# Revit family: ВКО прес_турбо_Eng
name_source: partatom
category: Mechanical Equipment
units: mm (PartAtom-declared; Revit-internal decimal feet)

## family parameters
Always vertical = Yes
Classification = None
Cut with Voids When Loaded = No
Part Type = Normal
Room Calculation Point = No
Round Connector Dimension = Use Diameter
Shared = No
Work Plane-Based = No

## types (6) — shared parameters
00_20_Manufacturer = Vents
00_20_Name = Axial fan
Casing Material = Plastic, opaque, white
Frequency = 50 Hz
Load Classification = HVAC
Maintenance zone material = <By Category>
Manufacturer = Vents
Number of Fase = 1
URL = https://ventilation-system.com
Voltage = 230 V
zero-valued in all types: Default Elevation

## per-type parameters (varying)
| type | Amperage | Apparent Load | D | D1 | Diameter | Dy | L | L1 | Length | Maximum Air Flow | Power | R | R1 | Ry | Sound pressure level at 3 m distance | Weight |
| 100 VKO press | 0.100 A | 23 W | 100 mm  [stored 0.328084 ft] | 104 mm | 100 mm  [stored 0.328084 ft] | 98 mm  [stored 0.321522 ft] | 91 mm  [stored 0.298556 ft] | 31 mm  [stored 0.101706 ft] | 91 mm  [stored 0.298556 ft] | 106.0 m³/h | 16 W | 50 mm  [stored 0.164042 ft] | 52 mm | 49 mm  [stored 0.160761 ft] | 39 dBA | 0.41 kg |
| 125 VKO press | 0.105 A | 24 W | 125 mm  [stored 0.410105 ft] | 129 mm | 125 mm  [stored 0.410105 ft] | 123 mm  [stored 0.403543 ft] | 93 mm  [stored 0.305118 ft] | 31 mm  [stored 0.101706 ft] | 93 mm  [stored 0.305118 ft] | 192.0 m³/h | 24 W | 63 mm | 65 mm | 62 mm | 39 dBA | 0.48 kg |
| 150 VKO press | 0.130 A | 30 W | 150 mm | 154 mm  [stored 0.505249 ft] | 150 mm | 148 mm  [stored 0.485564 ft] | 108 mm  [stored 0.354331 ft] | 46 mm  [stored 0.150919 ft] | 108 mm  [stored 0.354331 ft] | 312.0 m³/h | 29 W | 75 mm | 77 mm  [stored 0.252625 ft] | 74 mm  [stored 0.242782 ft] | 44 dBA | 0.80 kg |
| 100 VKO turbo | 0.100 A | 23 W | 100 mm  [stored 0.328084 ft] | 104 mm | 100 mm  [stored 0.328084 ft] | 98 mm  [stored 0.321522 ft] | 91 mm  [stored 0.298556 ft] | 31 mm  [stored 0.101706 ft] | 91 mm  [stored 0.298556 ft] | 135.0 m³/h | 16 W | 50 mm  [stored 0.164042 ft] | 52 mm | 49 mm  [stored 0.160761 ft] | 38 dBA | 0.41 kg |
| 125 VKO turbo | 0.105 A | 24 W | 125 mm  [stored 0.410105 ft] | 129 mm | 125 mm  [stored 0.410105 ft] | 123 mm  [stored 0.403543 ft] | 93 mm  [stored 0.305118 ft] | 31 mm  [stored 0.101706 ft] | 93 mm  [stored 0.305118 ft] | 243.0 m³/h | 24 W | 63 mm | 65 mm | 62 mm | 39 dBA | 0.48 kg |
| 150 VKO turbo | 0.130 A | 30 W | 150 mm | 154 mm  [stored 0.505249 ft] | 150 mm | 148 mm  [stored 0.485564 ft] | 108 mm  [stored 0.354331 ft] | 46 mm  [stored 0.150919 ft] | 108 mm  [stored 0.354331 ft] | 358.0 m³/h | 29 W | 75 mm | 77 mm  [stored 0.252625 ft] | 74 mm  [stored 0.242782 ft] | 44 dBA | 0.80 kg |

note: column(s) folded — value = type name in every type: 00_20_Type

note: [stored X ft] marks values corroborated as IEEE doubles in the binary element streams (Revit-internal decimal feet)
